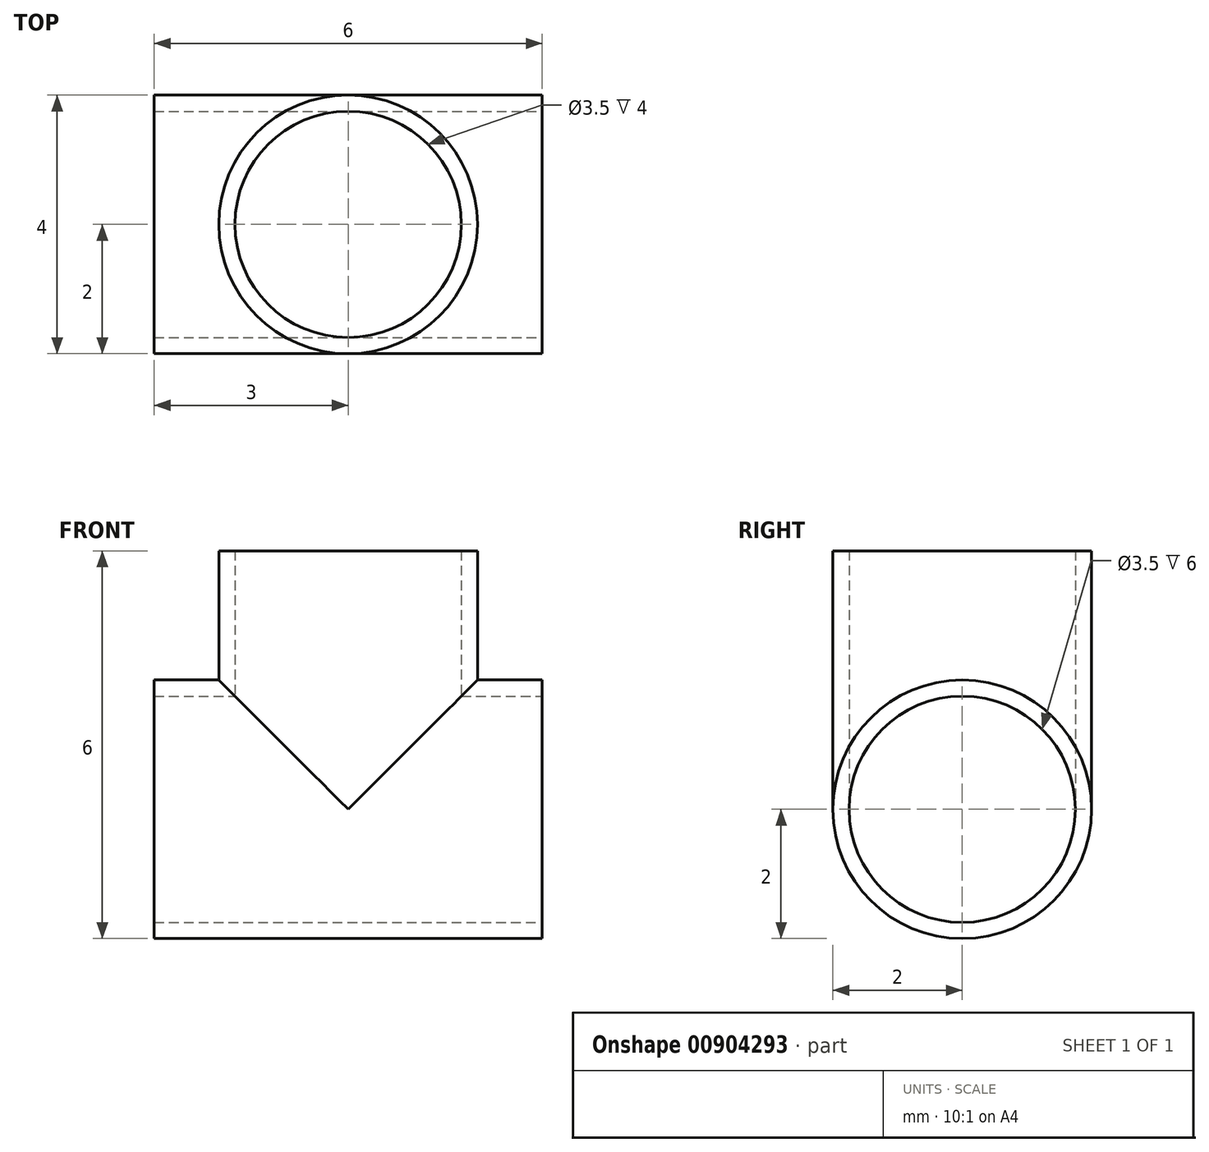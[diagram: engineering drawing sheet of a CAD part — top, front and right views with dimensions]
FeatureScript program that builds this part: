
annotation { "Feature Type Name" : "Feature", "Feature Type Description" : "" }
export const myFeature = defineFeature(function(context is Context, id is Id, definition is map)
    precondition{}
    {
        {
            var Q0;
            Q0=qCreatedBy(makeId("Top.planeOp"),FACE);
            var sketch = newSketch(context, id + "F0", { "sketchPlane" : qUnion([Q0])});
            skLineSegment(sketch, "E0.bottom", {"start": v(5, 0) * mm, "end": v(-5, 0) * mm});
            skLineSegment(sketch, "E0.top", {"start": v(5, 0) * mm, "end": v(-5, 0) * mm});
            skLineSegment(sketch, "E0.left", {"start": v(5, 0) * mm, "end": v(5, 0) * mm});
            skLineSegment(sketch, "E0.right", {"start": v(-5, 0) * mm, "end": v(-5, 0) * mm});
            skPoint(sketch, "E0.middle", {"position": v(0, 0) * mm});
            skCircle(sketch, "E1", {"center": v(-5, 0) * mm, "radius": 1.75 * mm});
            skCircle(sketch, "E2", {"center": v(-5, 0) * mm, "radius": 2 * mm});
            skCircle(sketch, "E3", {"center": v(5, 0) * mm, "radius": 1.75 * mm});
            skCircle(sketch, "E4", {"center": v(5, 0) * mm, "radius": 2 * mm});
            skSolve(sketch);
        }
        {
            var Q0;
            Q0=qCreatedBy(makeId("Front.planeOp"),FACE);
            var sketch = newSketch(context, id + "F1", { "sketchPlane" : qUnion([Q0])});
            skLineSegment(sketch, "E5.0", {"start": v(-7, 0) * mm, "end": v(-3, 0) * mm});
            skLineSegment(sketch, "E6.0", {"start": v(3, 0) * mm, "end": v(7, 0) * mm});
            skLineSegment(sketch, "E7", {"start": v(-3, 0) * mm, "end": v(-3, 4) * mm});
            skLineSegment(sketch, "E8", {"start": v(-3, 2) * mm, "end": v(-1.94, 2) * mm});
            skArc(sketch, "E9", {"start": v(-3, 2) * mm, "mid": v(-4.41, 1.41) * mm, "end": v(-5, 0) * mm});
            skLineSegment(sketch, "E10", {"start": v(0, 0) * mm, "end": v(0, 0.78) * mm});
            skLineSegment(sketch, "E11.MirrorCS", {"start": v(3, 0) * mm, "end": v(3, 4) * mm});
            skArc(sketch, "E12.MirrorCS", {"start": v(3, 2) * mm, "mid": v(4.41, 1.41) * mm, "end": v(5, 0) * mm});
            skSolve(sketch);
        }
        {
            var Q0;
            Q0=makeQuery(id+"F0.imprint","IMPRINT",FACE,{"disambiguationData":[TD([[makeQuery(id+"F0.imprint","IMPRINT",EDGE,{"derivedFrom":sQuery(id+"F0.wireOp",EDGE,"E1")}),-1.0]])]});
            var Q1;
            Q1=sQuery(id+"F1.wireOp",EDGE,"E9");
            sweep(context, id + "F2", {"profiles" : qUnion([Q0]), "path" : qUnion([Q1])});
        }
        {
            var Q0;
            Q0=makeQuery(id+"F0.imprint","IMPRINT",FACE,{"disambiguationData":[TD([[makeQuery(id+"F0.imprint","IMPRINT",EDGE,{"derivedFrom":sQuery(id+"F0.wireOp",EDGE,"E3")}),-1.0]])]});
            var Q1;
            Q1=sQuery(id+"F1.wireOp",EDGE,"E12.MirrorCS");
            sweep(context, id + "F3", {"profiles" : qUnion([Q0]), "path" : qUnion([Q1])});
        }
        {
            var Q0;
            Q0=makeQuery(id+"F3.opSweep","CAP_FACE",FACE,{"disambiguationData":[OSD([sQuery(id+"F0.wireOp",EDGE,"E3"),sQuery(id+"F0.wireOp",EDGE,"E4"),sQuery(id+"F1.wireOp",VERTEX,"E12.MirrorCS.start")])],"isStart":false});
            extrude(context, id + "F4", {"entities" : qUnion([Q0]), "operationType" : NewBodyOperationType.ADD, "depth" : 3 * mm, "offsetDistance" : 25 * mm});
        }
        {
            var Q0;
            Q0=makeQuery(id+"F2.opSweep","CAP_FACE",FACE,{"disambiguationData":[OSD([sQuery(id+"F0.wireOp",EDGE,"E1"),sQuery(id+"F0.wireOp",EDGE,"E2"),sQuery(id+"F1.wireOp",VERTEX,"E9.start")])],"isStart":false});
            extrude(context, id + "F5", {"entities" : qUnion([Q0]), "depth" : 3 * mm, "offsetDistance" : 25 * mm});
        }
        {
            var Q0;
            Q0=makeQuery(id+"F2.opSweep","SWEPT_BODY",BODY,{"disambiguationData":[OSD([sQuery(id+"F0.wireOp",EDGE,"E1"),sQuery(id+"F0.wireOp",EDGE,"E2"),sQuery(id+"F1.wireOp",EDGE,"E9")])]});
            var Q1;
            Q1=makeQuery(id+"F3.opSweep","SWEPT_BODY",BODY,{"disambiguationData":[OSD([sQuery(id+"F0.wireOp",EDGE,"E3"),sQuery(id+"F0.wireOp",EDGE,"E4"),sQuery(id+"F1.wireOp",EDGE,"E12.MirrorCS")])]});
            var Q2;
            Q2=makeQuery(id+"F5.opExtrude","SWEPT_BODY",BODY,{"disambiguationData":[OSD([sQuery(id+"F0.wireOp",EDGE,"E1"),sQuery(id+"F0.wireOp",EDGE,"E2"),sQuery(id+"F1.wireOp",VERTEX,"E9.start")])]});
            booleanBodies(context, id + "F6", {"operationType" : BooleanOperationType.UNION, "tools" : qUnion([Q0, Q1, Q2])});
        }
        {
            var Q0;
            Q0=qCreatedBy(makeId("Top.planeOp"),FACE);
            cPlane(context, id + "F7", {"entities" : qUnion([Q0]), "cplaneType" : CPlaneType.OFFSET, "offset" : 2 * mm, "width" : 150 * mm, "height" : 150 * mm});
        }
        {
            var Q0;
            Q0=qCreatedBy(id+"F7.planeOp",FACE);
            var sketch = newSketch(context, id + "F8", { "sketchPlane" : qUnion([Q0])});
            skCircle(sketch, "E13", {"center": v(0, 0) * mm, "radius": 2 * mm});
            skCircle(sketch, "E14", {"center": v(0, 0) * mm, "radius": 1.75 * mm});
            skSolve(sketch);
        }
        {
            var Q0;
            Q0=makeQuery(id+"F8.imprint","IMPRINT",FACE,{"disambiguationData":[TD([[makeQuery(id+"F8.imprint","IMPRINT",EDGE,{"derivedFrom":sQuery(id+"F8.wireOp",EDGE,"E13")}),1.0]])]});
            extrude(context, id + "F9", {"entities" : qUnion([Q0]), "operationType" : NewBodyOperationType.ADD, "depth" : 4 * mm, "offsetDistance" : 25 * mm});
        }
        {
            var Q0;
            Q0=makeQuery(id+"F9.opExtrude","CAP_FACE",FACE,{"disambiguationData":[OSD([sQuery(id+"F8.wireOp",EDGE,"E13"),sQuery(id+"F8.wireOp",EDGE,"E14")])],"isStart":false});
            var sketch = newSketch(context, id + "F10", { "sketchPlane" : qUnion([Q0])});
            skCircle(sketch, "E15.0", {"center": v(0, 0) * mm, "radius": 1.75 * mm});
            skSolve(sketch);
        }
        {
            var Q0;
            Q0=makeQuery(id+"F10.imprint","IMPRINT",FACE,{"disambiguationData":[TD([[makeQuery(id+"F10.imprint","IMPRINT",EDGE,{"derivedFrom":sQuery(id+"F10.wireOp",EDGE,"E15.0")}),1.0]])]});
            extrude(context, id + "F11", {"entities" : qUnion([Q0]), "operationType" : NewBodyOperationType.REMOVE, "oppositeDirection" : true, "depth" : 4 * mm, "offsetDistance" : 25 * mm});
        }
        {
            var Q0;
            Q0=qCreatedBy(makeId("Right.planeOp"),FACE);
            cPlane(context, id + "F12", {"entities" : qUnion([Q0]), "cplaneType" : CPlaneType.OFFSET, "offset" : 3 * mm, "width" : 150 * mm, "height" : 150 * mm});
        }
        {
            var Q0;
            Q0=qCreatedBy(id+"F12.planeOp",FACE);
            var sketch = newSketch(context, id + "F13", { "sketchPlane" : qUnion([Q0])});
            skCircle(sketch, "E16.0", {"center": v(0, 2) * mm, "radius": 2 * mm});
            skCircle(sketch, "E17", {"center": v(0, 2) * mm, "radius": 1.75 * mm});
            skSolve(sketch);
        }
        {
            var Q0;
            Q0=makeQuery(id+"F13.imprint","IMPRINT",FACE,{"disambiguationData":[TD([[makeQuery(id+"F13.imprint","IMPRINT",EDGE,{"derivedFrom":sQuery(id+"F13.wireOp",EDGE,"E17")}),1.0]])]});
            extrude(context, id + "F14", {"entities" : qUnion([Q0]), "operationType" : NewBodyOperationType.REMOVE, "oppositeDirection" : true, "depth" : 6 * mm, "offsetDistance" : 25 * mm});
        }
        {
            var Q0;
            Q0=makeQuery(id+"F2.opSweep","CAP_FACE",FACE,{"disambiguationData":[OSD([sQuery(id+"F0.wireOp",EDGE,"E1"),sQuery(id+"F0.wireOp",EDGE,"E2"),sQuery(id+"F1.wireOp",VERTEX,"E9.end")])],"isStart":true});
            var sketch = newSketch(context, id + "F15", { "sketchPlane" : qUnion([Q0])});
            skLineSegment(sketch, "E18.0", {"start": v(-3, 2) * mm, "end": v(-3, -2) * mm});
            skLineSegment(sketch, "E19", {"start": v(0, 0) * mm, "end": v(0, 1.29) * mm});
            skLineSegment(sketch, "E20.bottom", {"start": v(-3, 2) * mm, "end": v(-5, 2) * mm});
            skLineSegment(sketch, "E20.top", {"start": v(-3, -2) * mm, "end": v(-5, -2) * mm});
            skLineSegment(sketch, "E20.right", {"start": v(-5, 2) * mm, "end": v(-5, -2) * mm});
            skLineSegment(sketch, "E21.MirrorCS", {"start": v(3, 2) * mm, "end": v(3, -2) * mm});
            skLineSegment(sketch, "E22.MirrorCS", {"start": v(3, 2) * mm, "end": v(5, 2) * mm});
            skLineSegment(sketch, "E23.MirrorCS", {"start": v(5, 2) * mm, "end": v(5, -2) * mm});
            skLineSegment(sketch, "E24.MirrorCS", {"start": v(3, -2) * mm, "end": v(5, -2) * mm});
            skSolve(sketch);
        }
        {
            var Q0;
            {var subQ0=sQuery(id+"F15.wireOp",EDGE,"E20.right");var subQ1=sQuery(id+"F15.wireOp",EDGE,"E20.bottom");var subQ2=makeQuery(id+"F15.imprint","INTERSECT",VERTEX,{"derivedFrom":[subQ1,subQ0]});Q0=makeQuery(id+"F15.imprint","IMPRINT",FACE,{"disambiguationData":[TD([[makeQuery(id+"F15.imprint","IMPRINT",EDGE,{"disambiguationData":[TD([[subQ2,1.0]])],"derivedFrom":subQ1}),1.0]])]});}
            var Q1;
            {var subQ0=sQuery(id+"F15.wireOp",EDGE,"E18.0");var subQ1=sQuery(id+"F15.wireOp",EDGE,"E20.bottom");var subQ2=makeQuery(id+"F15.imprint","INTERSECT",VERTEX,{"derivedFrom":[subQ1,subQ0]});Q1=makeQuery(id+"F15.imprint","IMPRINT",FACE,{"disambiguationData":[TD([[makeQuery(id+"F15.imprint","IMPRINT",EDGE,{"disambiguationData":[TD([[subQ2,-1.0]])],"derivedFrom":subQ1}),1.0]])]});}
            var Q2;
            {var subQ0=sQuery(id+"F1.wireOp",VERTEX,"E9.end");Q2=makeQuery(id+"F15.imprint","IMPRINT",FACE,{"disambiguationData":[TD([[makeQuery(id+"F15.imprint","IMPRINT",EDGE,{"derivedFrom":makeQuery(id+"F2.opSweep","CAP_EDGE",EDGE,{"disambiguationData":[OSD([sQuery(id+"F0.wireOp",EDGE,"E1"),subQ0])],"isStart":true})}),1.0]])]});}
            var Q3;
            Q3=makeQuery(id+"F15.imprint","IMPRINT",FACE,{"disambiguationData":[TD([[makeQuery(id+"F15.imprint","IMPRINT",EDGE,{"derivedFrom":makeQuery(id+"F2.opSweep","CAP_EDGE",EDGE,{"disambiguationData":[OSD([sQuery(id+"F0.wireOp",EDGE,"E1"),sQuery(id+"F1.wireOp",VERTEX,"E9.end")])],"isStart":true})}),-1.0]])]});
            var Q4;
            {var subQ0=sQuery(id+"F15.wireOp",EDGE,"E18.0");var subQ1=sQuery(id+"F15.wireOp",EDGE,"E20.top");var subQ2=makeQuery(id+"F15.imprint","INTERSECT",VERTEX,{"derivedFrom":[subQ1,subQ0]});Q4=makeQuery(id+"F15.imprint","IMPRINT",FACE,{"disambiguationData":[TD([[makeQuery(id+"F15.imprint","IMPRINT",EDGE,{"disambiguationData":[TD([[subQ2,-1.0]])],"derivedFrom":subQ1}),-1.0]])]});}
            var Q5;
            {var subQ0=sQuery(id+"F15.wireOp",EDGE,"E20.right");var subQ1=sQuery(id+"F15.wireOp",EDGE,"E20.top");var subQ2=makeQuery(id+"F15.imprint","INTERSECT",VERTEX,{"derivedFrom":[subQ1,subQ0]});Q5=makeQuery(id+"F15.imprint","IMPRINT",FACE,{"disambiguationData":[TD([[makeQuery(id+"F15.imprint","IMPRINT",EDGE,{"disambiguationData":[TD([[subQ2,1.0]])],"derivedFrom":subQ1}),-1.0]])]});}
            var Q6;
            {var subQ0=sQuery(id+"F1.wireOp",VERTEX,"E9.end");var subQ3=sQuery(id+"F15.wireOp",EDGE,"E20.right");var subQ6=makeQuery(id+"F2.opSweep","CAP_EDGE",EDGE,{"disambiguationData":[OSD([sQuery(id+"F0.wireOp",EDGE,"E1"),subQ0])],"isStart":true});var subQ8=makeQuery(id+"F15.imprint","INTERSECT",VERTEX,{"disambiguationData":[OD(0.0)],"derivedFrom":[subQ6,subQ3]});Q6=makeQuery(id+"F15.imprint","IMPRINT",FACE,{"disambiguationData":[TD([[makeQuery(id+"F15.imprint","IMPRINT",EDGE,{"disambiguationData":[TD([[subQ8,1.0]])],"derivedFrom":subQ3}),1.0]])]});}
            var Q7;
            Q7=makeQuery(id+"F3.opSweep","CAP_FACE",FACE,{"disambiguationData":[OSD([sQuery(id+"F0.wireOp",EDGE,"E3"),sQuery(id+"F0.wireOp",EDGE,"E4"),sQuery(id+"F1.wireOp",VERTEX,"E12.MirrorCS.end")])],"isStart":true});
            var Q8;
            Q8=makeQuery(id+"F15.imprint","IMPRINT",FACE,{"disambiguationData":[TD([[makeQuery(id+"F15.imprint","IMPRINT",EDGE,{"derivedFrom":sQuery(id+"F15.wireOp",EDGE,"E21.MirrorCS")}),1.0]])]});
            extrude(context, id + "F16", {"entities" : qUnion([Q0, Q1, Q2, Q3, Q4, Q5, Q6, Q7, Q8]), "operationType" : NewBodyOperationType.REMOVE, "oppositeDirection" : true, "depth" : 25 * mm, "offsetDistance" : 25 * mm});
        }
        {
            var Q0;
            Q0=makeQuery(id+"F16.boolean.opBoolean","COPY",FACE,{"derivedFrom":makeQuery(id+"F16.opExtrude","SWEPT_FACE",FACE,{"disambiguationData":[OSD([sQuery(id+"F15.wireOp",EDGE,"E23.MirrorCS")])]})});
            var sketch = newSketch(context, id + "F17", { "sketchPlane" : qUnion([Q0])});
            skLineSegment(sketch, "E25", {"start": v(1.75, 2.2) * mm, "end": v(-1.75, 2.2) * mm});
            skSolve(sketch);
        }
        {
            var Q0;
            {var subQ1=makeQuery(id+"F16.opExtrude","SWEPT_FACE",FACE,{"disambiguationData":[OSD([sQuery(id+"F15.wireOp",EDGE,"E23.MirrorCS")])]});var subQ4=sQuery(id+"F1.wireOp",EDGE,"E12.MirrorCS");var subQ5=makeQuery(id+"F16.boolean.opBoolean","INTERSECT",EDGE,{"derivedFrom":[makeQuery(id+"F3.opSweep","SWEPT_FACE",FACE,{"disambiguationData":[OSD([sQuery(id+"F0.wireOp",EDGE,"E4"),subQ4])]}),subQ1]});Q0=makeQuery(id+"F17.imprint","IMPRINT",FACE,{"disambiguationData":[TD([[makeQuery(id+"F17.imprint","IMPRINT",EDGE,{"derivedFrom":subQ5}),-1.0]])]});}
            extrude(context, id + "F18", {"entities" : qUnion([Q0]), "operationType" : NewBodyOperationType.REMOVE, "oppositeDirection" : true, "depth" : 25 * mm, "offsetDistance" : 25 * mm});
        }
        {
            var Q0;
            {var subQ0=sQuery(id+"F17.wireOp",EDGE,"E25");var subQ1=makeQuery(id+"F16.opExtrude","SWEPT_FACE",FACE,{"disambiguationData":[OSD([sQuery(id+"F15.wireOp",EDGE,"E23.MirrorCS")])]});var subQ2=sQuery(id+"F0.wireOp",EDGE,"E3");var subQ3=sQuery(id+"F1.wireOp",EDGE,"E12.MirrorCS");Q0=makeQuery(id+"F18.boolean.opBoolean","COPY",FACE,{"derivedFrom":makeQuery(id+"F18.opExtrude","SWEPT_FACE",FACE,{"disambiguationData":[OSD([subQ0]),TDD([makeQuery(id+"F17.imprint","IMPRINT",EDGE,{"disambiguationData":[TD([[makeQuery(id+"F17.imprint","INTERSECT",VERTEX,{"disambiguationData":[OD(1.0)],"derivedFrom":[makeQuery(id+"F16.boolean.opBoolean","INTERSECT",EDGE,{"derivedFrom":[makeQuery(id+"F3.opSweep","SWEPT_FACE",FACE,{"disambiguationData":[OSD([subQ2,subQ3])]}),subQ1]}),subQ0]}),-1.0]])],"derivedFrom":subQ0})])]})});}
            var sketch = newSketch(context, id + "F19", { "sketchPlane" : qUnion([Q0])});
            skLineSegment(sketch, "E26.bottom", {"start": v(5, 1.75) * mm, "end": v(6.87, 1.75) * mm});
            skLineSegment(sketch, "E26.top", {"start": v(5, -2.28) * mm, "end": v(6.87, -2.28) * mm});
            skLineSegment(sketch, "E26.left", {"start": v(5, 1.75) * mm, "end": v(5, -2.28) * mm});
            skLineSegment(sketch, "E26.right", {"start": v(6.87, 1.75) * mm, "end": v(6.87, -2.28) * mm});
            skSolve(sketch);
        }
        {
            var Q0;
            Q0=makeQuery(id+"F19.imprint","IMPRINT",FACE,{"disambiguationData":[TD([[makeQuery(id+"F19.imprint","IMPRINT",EDGE,{"derivedFrom":sQuery(id+"F19.wireOp",EDGE,"E26.bottom")}),-1.0]])]});
            var Q1;
            {var subQ1=sQuery(id+"F17.wireOp",EDGE,"E25");var subQ2=sQuery(id+"F15.wireOp",EDGE,"E23.MirrorCS");var subQ3=makeQuery(id+"F16.opExtrude","SWEPT_FACE",FACE,{"disambiguationData":[OSD([subQ2])]});var subQ4=sQuery(id+"F0.wireOp",EDGE,"E3");var subQ5=sQuery(id+"F1.wireOp",EDGE,"E12.MirrorCS");var subQ7=makeQuery(id+"F17.imprint","INTERSECT",VERTEX,{"disambiguationData":[OD(1.0)],"derivedFrom":[makeQuery(id+"F16.boolean.opBoolean","INTERSECT",EDGE,{"derivedFrom":[makeQuery(id+"F3.opSweep","SWEPT_FACE",FACE,{"disambiguationData":[OSD([subQ4,subQ5])]}),subQ3]}),subQ1]});var subQ9=makeQuery(id+"F18.boolean.opBoolean","COPY",EDGE,{"derivedFrom":makeQuery(id+"F18.opExtrude","SWEPT_EDGE",EDGE,{"disambiguationData":[OSD([subQ4,subQ5,subQ2,subQ1]),TDD([subQ7])]})});Q1=makeQuery(id+"F19.imprint","IMPRINT",FACE,{"disambiguationData":[TD([[makeQuery(id+"F19.imprint","IMPRINT",EDGE,{"derivedFrom":subQ9}),1.0]])]});}
            extrude(context, id + "F20", {"entities" : qUnion([Q0, Q1]), "operationType" : NewBodyOperationType.REMOVE, "oppositeDirection" : true, "depth" : 25 * mm, "offsetDistance" : 25 * mm});
        }
        {
            var Q0;
            Q0=makeQuery(id+"F19.imprint","IMPRINT",FACE,{"disambiguationData":[TD([[makeQuery(id+"F19.imprint","IMPRINT",EDGE,{"derivedFrom":sQuery(id+"F19.wireOp",EDGE,"E26.bottom")}),-1.0]])]});
            extrude(context, id + "F21", {"entities" : qUnion([Q0]), "operationType" : NewBodyOperationType.REMOVE, "depth" : 25 * mm, "offsetDistance" : 25 * mm});
        }
    });
